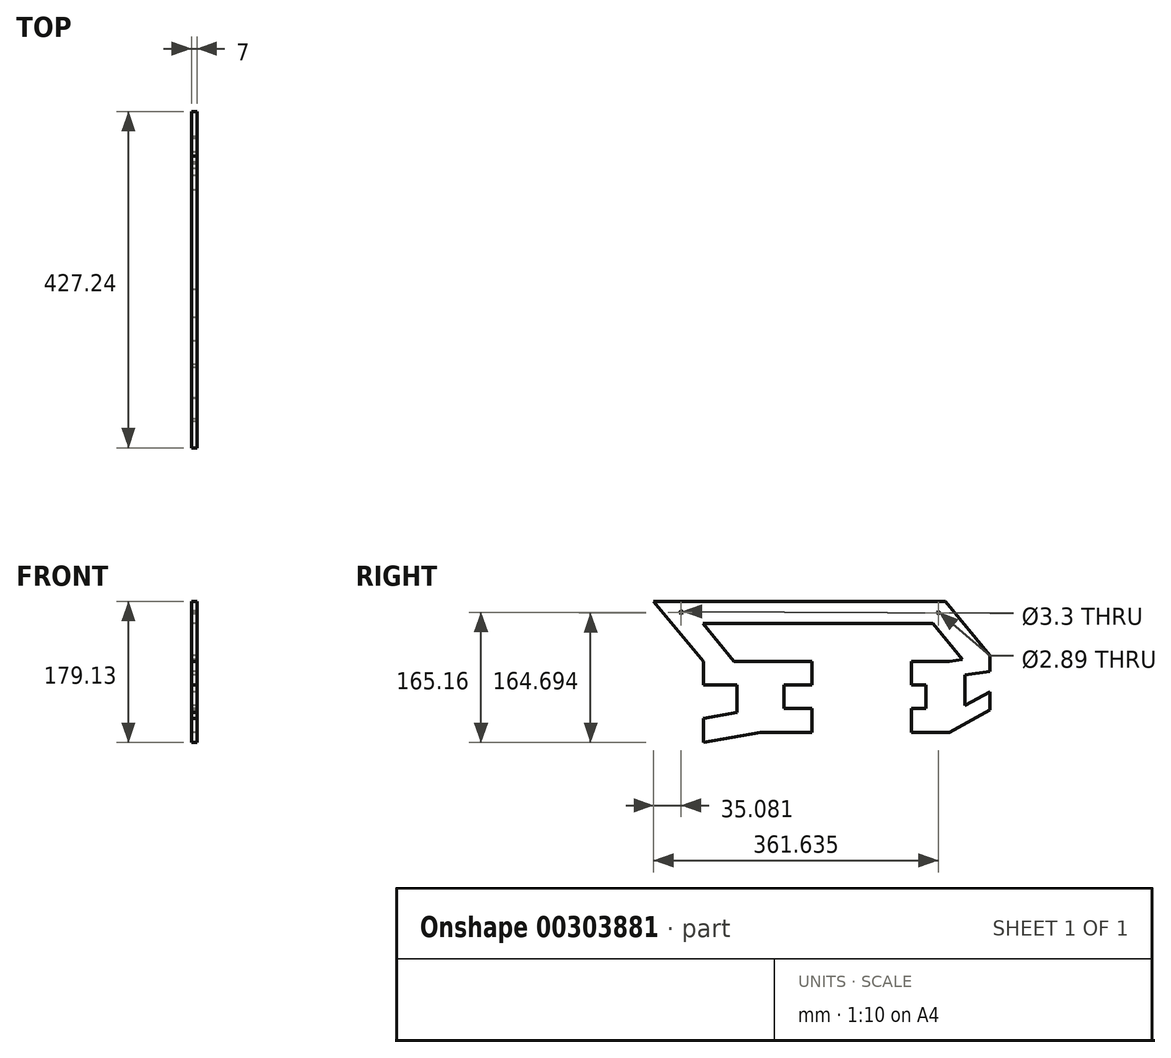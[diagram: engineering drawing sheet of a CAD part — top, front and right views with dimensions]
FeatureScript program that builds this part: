
annotation { "Feature Type Name" : "Feature", "Feature Type Description" : "" }
export const myFeature = defineFeature(function(context is Context, id is Id, definition is map)
    precondition{}
    {
        {
            var Q0;
            Q0=qCreatedBy(makeId("Right.planeOp"),FACE);
            var sketch = newSketch(context, id + "F0", { "sketchPlane" : qUnion([Q0])});
            skLineSegment(sketch, "E0.top", {"start": v(-356.9, -24.33) * mm, "end": v(-284.4, -11.55) * mm});
            skLineSegment(sketch, "E1.2", {"start": v(-314.4, 48.45) * mm, "end": v(-314.4, 13.63) * mm});
            skLineSegment(sketch, "E2.trimOffspring", {"start": v(-356.9, 48.45) * mm, "end": v(-314.4, 48.45) * mm});
            skLineSegment(sketch, "E3.trimOffspring", {"start": v(-356.9, 6.13) * mm, "end": v(-314.4, 13.63) * mm});
            skLineSegment(sketch, "E4.bottom", {"start": v(-317.95, 78.45) * mm, "end": v(-219.07, 78.45) * mm});
            skLineSegment(sketch, "E5.0", {"start": v(-254.4, 48.45) * mm, "end": v(-254.4, 18.45) * mm});
            skLineSegment(sketch, "E5.1", {"start": v(-254.4, 48.45) * mm, "end": v(-219.07, 48.45) * mm});
            skLineSegment(sketch, "E5.3", {"start": v(-254.4, 18.45) * mm, "end": v(-219.07, 18.45) * mm});
            skLineSegment(sketch, "E6", {"start": v(-356.9, 78.45) * mm, "end": v(-356.9, 48.45) * mm});
            skLineSegment(sketch, "E7", {"start": v(-219.07, 48.45) * mm, "end": v(-219.07, 78.45) * mm});
            skLineSegment(sketch, "E8", {"start": v(-219.07, 18.45) * mm, "end": v(-219.07, -11.55) * mm});
            skLineSegment(sketch, "E9", {"start": v(-219.07, -11.55) * mm, "end": v(-284.4, -11.55) * mm});
            skLineSegment(sketch, "E10", {"start": v(-356.9, 6.13) * mm, "end": v(-356.9, -24.33) * mm});
            skLineSegment(sketch, "E11.bottom", {"start": v(-44.4, 78.45) * mm, "end": v(7.13, 86.12) * mm});
            skLineSegment(sketch, "E11.left", {"start": v(-44.4, 78.45) * mm, "end": v(-44.4, -11.55) * mm});
            skLineSegment(sketch, "E12", {"start": v(-44.4, -11.55) * mm, "end": v(7.13, 17.06) * mm});
            skLineSegment(sketch, "E13.1", {"start": v(-24.4, 61.21) * mm, "end": v(7.13, 65.9) * mm});
            skLineSegment(sketch, "E13.3", {"start": v(-24.4, 22.43) * mm, "end": v(7.13, 39.93) * mm});
            skLineSegment(sketch, "E13.4", {"start": v(-24.4, 61.21) * mm, "end": v(-24.4, 22.43) * mm});
            skLineSegment(sketch, "E14.bottom", {"start": v(-92.87, 78.45) * mm, "end": v(-44.4, 78.45) * mm});
            skLineSegment(sketch, "E14.top", {"start": v(-92.87, -11.55) * mm, "end": v(-44.4, -11.55) * mm});
            skLineSegment(sketch, "E15.trimOffspring", {"start": v(-92.87, 48.45) * mm, "end": v(-74.4, 48.45) * mm});
            skLineSegment(sketch, "E16.trimOffspring", {"start": v(-92.87, 18.45) * mm, "end": v(-74.4, 18.45) * mm});
            skLineSegment(sketch, "E17", {"start": v(-92.87, 78.45) * mm, "end": v(-92.87, 48.45) * mm});
            skLineSegment(sketch, "E18", {"start": v(-74.4, 18.45) * mm, "end": v(-92.87, 18.45) * mm});
            skLineSegment(sketch, "E19", {"start": v(-92.87, 18.45) * mm, "end": v(-92.87, -11.55) * mm});
            skLineSegment(sketch, "E20", {"start": v(7.13, 39.93) * mm, "end": v(-24.4, 22.43) * mm});
            skLineSegment(sketch, "E21", {"start": v(-24.4, 61.21) * mm, "end": v(6.7, 65.84) * mm});
            skLineSegment(sketch, "E22", {"start": v(7.13, 86.12) * mm, "end": v(7.13, 65.9) * mm});
            skLineSegment(sketch, "E23.trimOffspring", {"start": v(7.13, 39.93) * mm, "end": v(7.13, 17.06) * mm});
            skLineSegment(sketch, "E24.right", {"start": v(-284.4, 78.45) * mm, "end": v(-284.4, -11.55) * mm});
            skLineSegment(sketch, "E25.bottom", {"start": v(-284.4, 78.45) * mm, "end": v(-219.07, 78.45) * mm});
            skLineSegment(sketch, "E25.top", {"start": v(-284.4, -11.55) * mm, "end": v(-219.07, -11.55) * mm});
            skLineSegment(sketch, "E26.2", {"start": v(-74.4, 48.45) * mm, "end": v(-74.4, 18.45) * mm});
            skLineSegment(sketch, "E27", {"start": v(-356.9, 78.45) * mm, "end": v(-420.11, 154.8) * mm});
            skLineSegment(sketch, "E28.1", {"start": v(-357.73, 126.5) * mm, "end": v(-123.13, 126.5) * mm});
            skLineSegment(sketch, "E28.2", {"start": v(-317.95, 78.45) * mm, "end": v(-357.73, 126.5) * mm});
            skCircle(sketch, "E29", {"center": v(-385.03, 140.83) * mm, "radius": 1.65 * mm});
            skLineSegment(sketch, "E30", {"start": v(-420.11, 154.8) * mm, "end": v(-49.74, 154.8) * mm});
            skLineSegment(sketch, "E31", {"start": v(-49.74, 154.8) * mm, "end": v(7.13, 86.12) * mm});
            skLineSegment(sketch, "E32.0", {"start": v(-65.25, 126.5) * mm, "end": v(-27.55, 80.96) * mm});
            skLineSegment(sketch, "E33", {"start": v(-123.13, 126.5) * mm, "end": v(-65.25, 126.5) * mm});
            skCircle(sketch, "E34", {"center": v(-58.47, 140.36) * mm, "radius": 1.45 * mm});
            skSolve(sketch);
        }
        {
            var Q0;
            Q0=makeQuery(id+"F0.imprint","IMPRINT",FACE,{"disambiguationData":[TD([[makeQuery(id+"F0.imprint","IMPRINT",EDGE,{"derivedFrom":sQuery(id+"F0.wireOp",EDGE,"E0.top")}),1.0]])]});
            var Q1;
            Q1=makeQuery(id+"F0.imprint","IMPRINT",FACE,{"disambiguationData":[TD([[makeQuery(id+"F0.imprint","IMPRINT",EDGE,{"derivedFrom":sQuery(id+"F0.wireOp",EDGE,"E7")}),1.0]])]});
            var Q2;
            Q2=makeQuery(id+"F0.imprint","IMPRINT",FACE,{"disambiguationData":[TD([[makeQuery(id+"F0.imprint","IMPRINT",EDGE,{"derivedFrom":sQuery(id+"F0.wireOp",EDGE,"E17")}),1.0]])]});
            var Q3;
            Q3=makeQuery(id+"F0.imprint","IMPRINT",FACE,{"disambiguationData":[TD([[makeQuery(id+"F0.imprint","IMPRINT",EDGE,{"derivedFrom":sQuery(id+"F0.wireOp",EDGE,"E12")}),1.0]])]});
            extrude(context, id + "F1", {"entities" : qUnion([Q0, Q1, Q2, Q3]), "depth" : 7 * mm});
        }
    });
